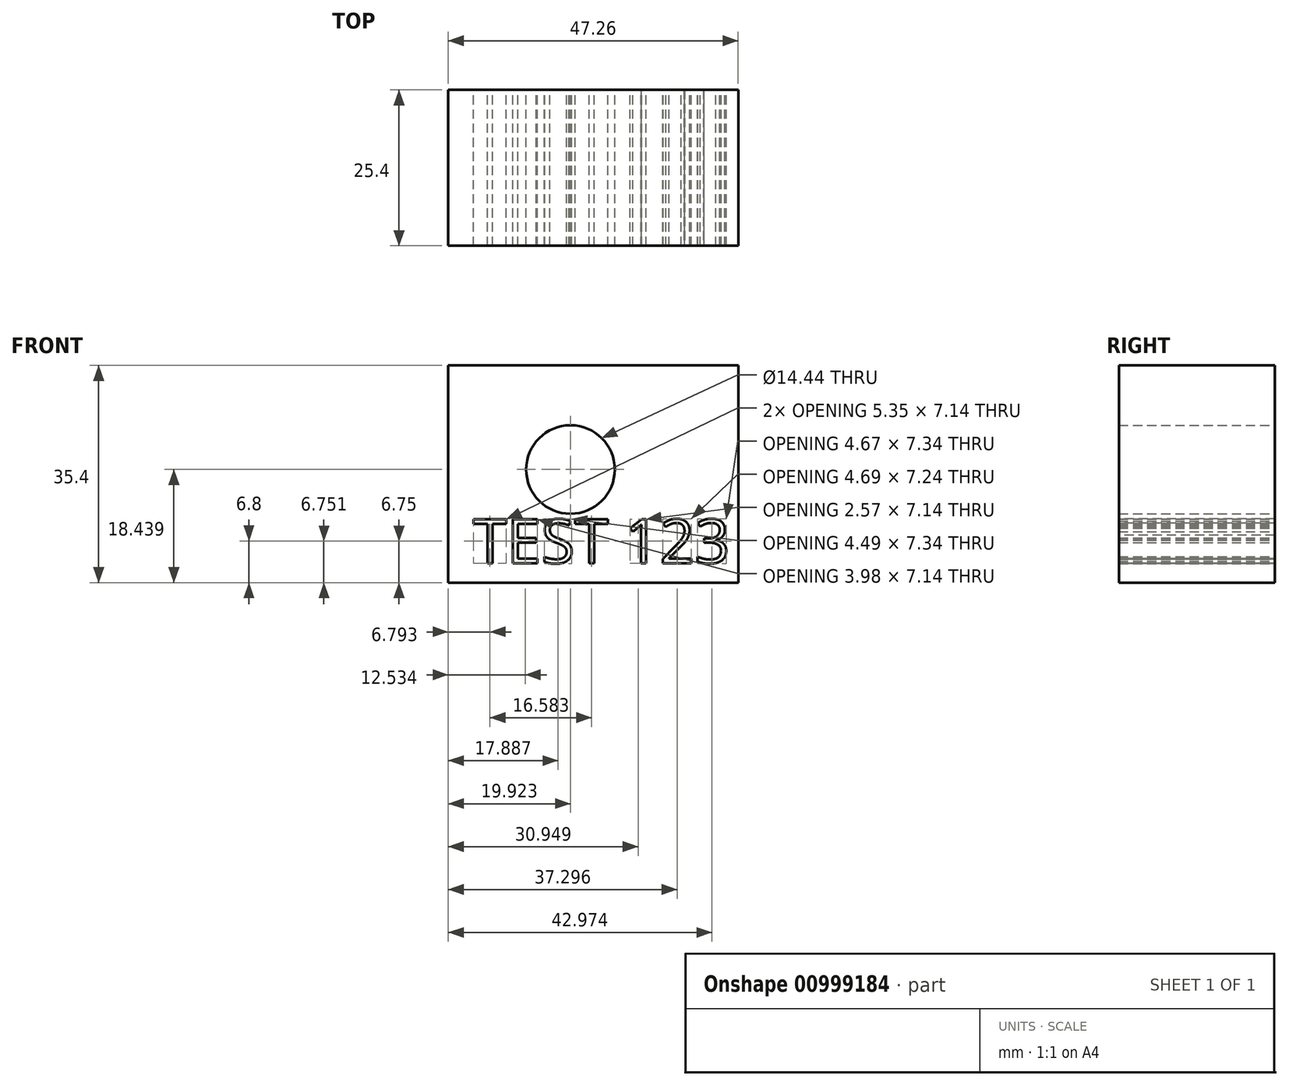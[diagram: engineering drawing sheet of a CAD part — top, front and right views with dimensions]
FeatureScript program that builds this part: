
annotation { "Feature Type Name" : "Feature", "Feature Type Description" : "" }
export const myFeature = defineFeature(function(context is Context, id is Id, definition is map)
    precondition{}
    {
        {
            var Q0;
            Q0=qCreatedBy(makeId("Front.planeOp"),FACE);
            var sketch = newSketch(context, id + "F0", { "sketchPlane" : qUnion([Q0])});
            skLineSegment(sketch, "E0.bottom", {"start": v(0, 0) * mm, "end": v(47.26, 0) * mm});
            skLineSegment(sketch, "E0.top", {"start": v(0, 35.4) * mm, "end": v(47.26, 35.4) * mm});
            skLineSegment(sketch, "E0.left", {"start": v(0, 0) * mm, "end": v(0, 35.4) * mm});
            skLineSegment(sketch, "E0.right", {"start": v(47.26, 0) * mm, "end": v(47.26, 35.4) * mm});
            skCircle(sketch, "E1", {"center": v(19.92, 18.44) * mm, "radius": 7.22 * mm});
            skText(sketch, "E2", { "text": "TEST 123", "fontName": "OpenSans-Regular.ttf"});
            const initialGuessF0  = {"E2": [0.00403, 0.00318, 1, 0, 0.0072]};
            skSetInitialGuess(sketch, initialGuessF0);
            skSolve(sketch);
        }
        {
            var Q0;
            Q0 = qSketchRegion(id + "F0", true);
            extrude(context, id + "F1", {"entities" : qUnion([Q0]), "depth" : 25.4 * mm, "offsetDistance" : 25.4 * mm});
        }
    });
